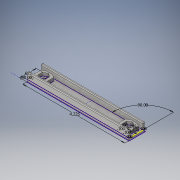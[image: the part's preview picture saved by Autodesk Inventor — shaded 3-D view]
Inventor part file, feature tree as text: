
AUTODESK INVENTOR PART (.ipt)
format: ipt  version: 2016 (Build 200138000, 138)  size: 212,992 bytes
history: native  units: in
note: dims shown in document units (in); Inventor stores cm internally (conversion verified against a paired STEP export)
features: extrude x3, sketch x2, hole x2, fillet x1
ambient origin geometry x8: Origin, YZ Plane, XZ Plane, XY Plane, X Axis, Y Axis, Z Axis, Center Point
bodies: Solid1 (feature_tree)
feature tree (8):
  extrude  "Extrusion1"  Depth=0.675in
  sketch  "Sketch2"  dims[d2=90.0deg d3=0.1in d4=0.0in d5=0.3625in d6=0.15in d7=0.75in d8=0.375in d9=0.25in d10=0.5635in d11=1.0in d12=0.8108in d16=0.1in d17=90.0deg d18=0.1in d20=0.222in d23=0.25in d24=0.0in d30=0.186in d33=0.125in d34=0.0in d35=0.15in d36=0.75in d37=0.375in d38=0.25in d39=0.5635in d40=1.0in d41=0.8108in d42=0.031in d43=0.1in d44=0.1in d45=0.1in d46=0.1in]
  hole  "Hole1"  [1 undecoded]
  extrude  "Extrusion2"  Depth=0.1in
  extrude  "Extrusion4"  Depth=0.1in
  hole  "Hole2"  [1 undecoded]
  fillet  "Fillet1"  Radius=0.1in
  sketch  "Sketch1"  dims[d0=4.225in d1=0.675in]
note: 2 required parameter values undecoded (feature->parameter linkage not recoverable at this tier; creation-order binding heuristic only, values carry confidence <= 0.55)
